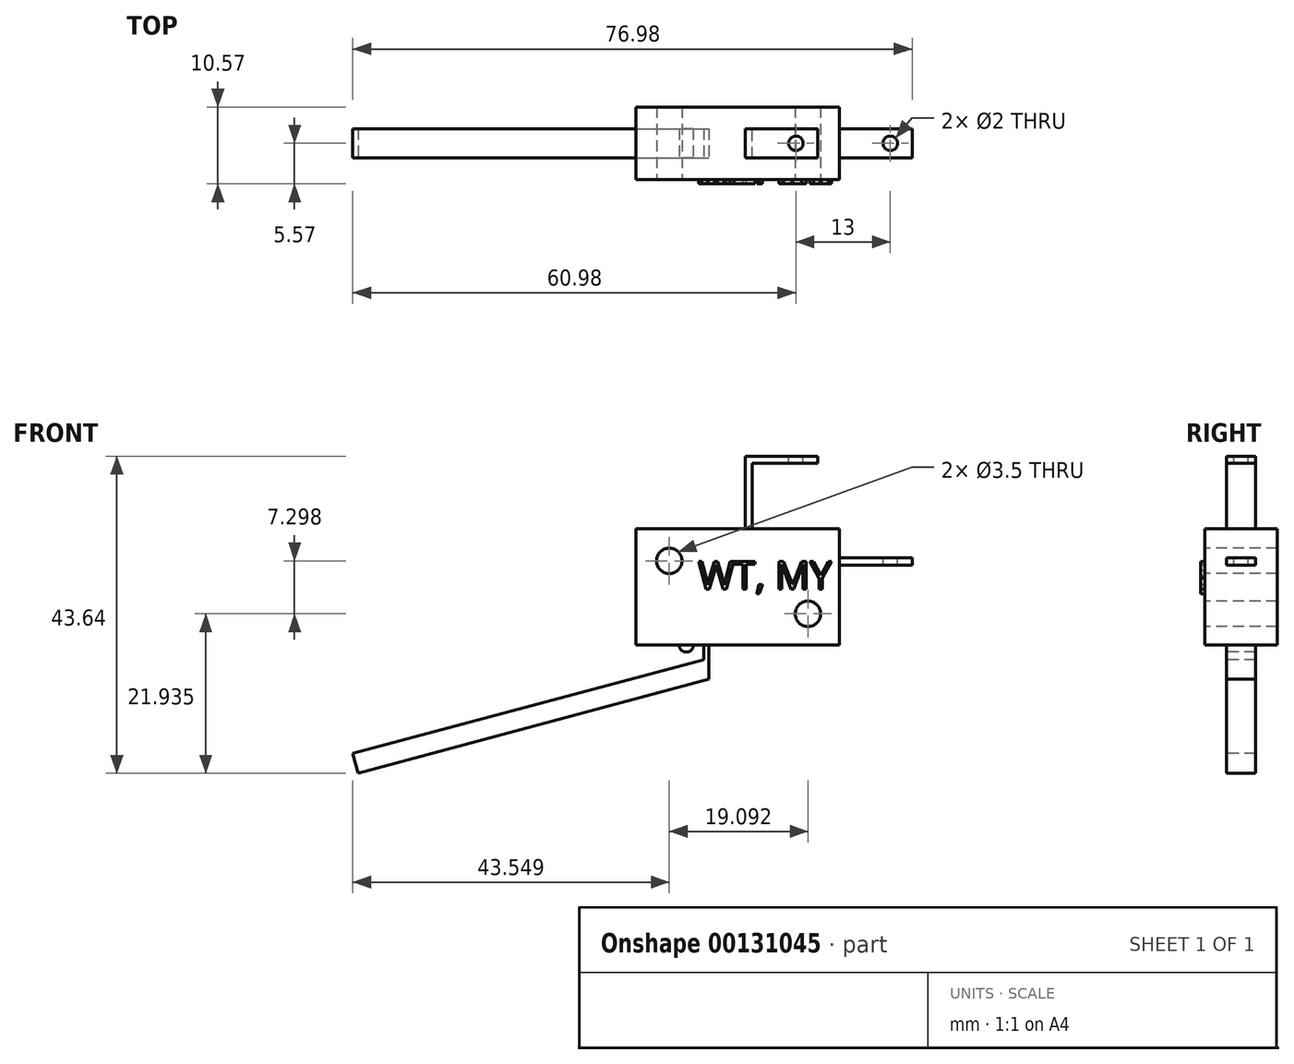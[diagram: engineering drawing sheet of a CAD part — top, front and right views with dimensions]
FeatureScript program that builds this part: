
annotation { "Feature Type Name" : "Feature", "Feature Type Description" : "" }
export const myFeature = defineFeature(function(context is Context, id is Id, definition is map)
    precondition{}
    {
        {
            var Q0;
            Q0=qCreatedBy(makeId("Front.planeOp"),FACE);
            var sketch = newSketch(context, id + "F0", { "sketchPlane" : qUnion([Q0])});
            skLineSegment(sketch, "E0.bottom", {"start": v(0, -16) * mm, "end": v(28, -16) * mm});
            skLineSegment(sketch, "E0.top", {"start": v(0, 0) * mm, "end": v(28, 0) * mm});
            skLineSegment(sketch, "E0.left", {"start": v(0, -16) * mm, "end": v(0, 0) * mm});
            skLineSegment(sketch, "E0.right", {"start": v(28, -16) * mm, "end": v(28, 0) * mm});
            skSolve(sketch);
        }
        {
            var Q0;
            Q0=qSketchRegion(id+"F0",true);
            extrude(context, id + "F1", {"entities" : qUnion([Q0]), "endBound" : BoundingType.SYMMETRIC, "depth" : 10 * mm});
        }
        {
            var Q0;
            Q0=makeQuery(id+"F1.opExtrude","CAP_FACE",FACE,{"disambiguationData":[OSD([sQuery(id+"F0.wireOp",EDGE,"E0.bottom"),sQuery(id+"F0.wireOp",EDGE,"E0.top"),sQuery(id+"F0.wireOp",EDGE,"E0.left"),sQuery(id+"F0.wireOp",EDGE,"E0.right")])],"isStart":false});
            var sketch = newSketch(context, id + "F2", { "sketchPlane" : qUnion([Q0])});
            skCircle(sketch, "E1", {"center": v(23.66, -11.7) * mm, "radius": 1.75 * mm});
            skCircle(sketch, "E2", {"center": v(4.57, -4.4) * mm, "radius": 1.75 * mm});
            skPoint(sketch, "E3", {"position": v(0, -8) * mm});
            skSolve(sketch);
        }
        {
            var Q0;
            Q0=makeQuery(id+"F2.imprint","IMPRINT",FACE,{"disambiguationData":[TD([[makeQuery(id+"F2.imprint","IMPRINT",EDGE,{"derivedFrom":sQuery(id+"F2.wireOp",EDGE,"E2")}),1.0]])]});
            var Q1;
            Q1=makeQuery(id+"F2.imprint","IMPRINT",FACE,{"disambiguationData":[TD([[makeQuery(id+"F2.imprint","IMPRINT",EDGE,{"derivedFrom":sQuery(id+"F2.wireOp",EDGE,"E1")}),1.0]])]});
            extrude(context, id + "F3", {"entities" : qUnion([Q0, Q1]), "operationType" : NewBodyOperationType.REMOVE, "endBound" : BoundingType.THROUGH_ALL, "oppositeDirection" : true, "depth" : 25 * mm});
        }
        {
            var Q0;
            Q0=makeQuery(id+"F1.opExtrude","SWEPT_FACE",FACE,{"disambiguationData":[OSD([sQuery(id+"F0.wireOp",EDGE,"E0.right")])]});
            var sketch = newSketch(context, id + "F4", { "sketchPlane" : qUnion([Q0])});
            skLineSegment(sketch, "E4.bottom", {"start": v(-2, -4) * mm, "end": v(2, -4) * mm});
            skLineSegment(sketch, "E4.top", {"start": v(-2, -5) * mm, "end": v(2, -5) * mm});
            skLineSegment(sketch, "E4.left", {"start": v(-2, -4) * mm, "end": v(-2, -5) * mm});
            skLineSegment(sketch, "E4.right", {"start": v(2, -4) * mm, "end": v(2, -5) * mm});
            skPoint(sketch, "E5", {"position": v(0, -5) * mm});
            skSolve(sketch);
        }
        {
            var Q0;
            Q0=qSketchRegion(id+"F4",true);
            extrude(context, id + "F5", {"entities" : qUnion([Q0]), "operationType" : NewBodyOperationType.ADD, "depth" : 10 * mm});
        }
        {
            var Q0;
            Q0=makeQuery(id+"F1.opExtrude","SWEPT_FACE",FACE,{"disambiguationData":[OSD([sQuery(id+"F0.wireOp",EDGE,"E0.top")])]});
            var sketch = newSketch(context, id + "F6", { "sketchPlane" : qUnion([Q0])});
            skLineSegment(sketch, "E6.bottom", {"start": v(15, -2) * mm, "end": v(16, -2) * mm});
            skLineSegment(sketch, "E6.top", {"start": v(15, 2) * mm, "end": v(16, 2) * mm});
            skLineSegment(sketch, "E6.left", {"start": v(15, -2) * mm, "end": v(15, 2) * mm});
            skLineSegment(sketch, "E6.right", {"start": v(16, -2) * mm, "end": v(16, 2) * mm});
            skSolve(sketch);
        }
        {
            var Q0;
            Q0=qSketchRegion(id+"F6",true);
            extrude(context, id + "F7", {"entities" : qUnion([Q0]), "operationType" : NewBodyOperationType.ADD, "depth" : 10 * mm});
        }
        {
            var Q0;
            Q0=makeQuery(id+"F7.opExtrude","SWEPT_FACE",FACE,{"disambiguationData":[OSD([sQuery(id+"F6.wireOp",EDGE,"E6.right")])]});
            var sketch = newSketch(context, id + "F8", { "sketchPlane" : qUnion([Q0])});
            skLineSegment(sketch, "E7.bottom", {"start": v(-2, 9) * mm, "end": v(2, 9) * mm});
            skLineSegment(sketch, "E7.top", {"start": v(-2, 10) * mm, "end": v(2, 10) * mm});
            skLineSegment(sketch, "E7.left", {"start": v(-2, 9) * mm, "end": v(-2, 10) * mm});
            skLineSegment(sketch, "E7.right", {"start": v(2, 9) * mm, "end": v(2, 10) * mm});
            skSolve(sketch);
        }
        {
            var Q0;
            Q0=qSketchRegion(id+"F8",true);
            extrude(context, id + "F9", {"entities" : qUnion([Q0]), "operationType" : NewBodyOperationType.ADD, "depth" : 9 * mm});
        }
        {
            var Q0;
            Q0=makeQuery(id+"F5.opExtrude","SWEPT_FACE",FACE,{"disambiguationData":[OSD([sQuery(id+"F4.wireOp",EDGE,"E4.bottom")])]});
            var sketch = newSketch(context, id + "F10", { "sketchPlane" : qUnion([Q0])});
            skCircle(sketch, "E8", {"center": v(35, 0) * mm, "radius": 1 * mm});
            skPoint(sketch, "E9", {"position": v(38, 0) * mm});
            skSolve(sketch);
        }
        {
            var Q0;
            Q0=qSketchRegion(id+"F10",true);
            extrude(context, id + "F11", {"entities" : qUnion([Q0]), "operationType" : NewBodyOperationType.REMOVE, "endBound" : BoundingType.THROUGH_ALL, "oppositeDirection" : true, "depth" : 25 * mm});
        }
        {
            var Q0;
            Q0=makeQuery(id+"F9.boolean.opBoolean","MERGE",FACE,{"derivedFrom":[makeQuery(id+"F7.opExtrude","CAP_FACE",FACE,{"disambiguationData":[OSD([sQuery(id+"F6.wireOp",EDGE,"E6.bottom"),sQuery(id+"F6.wireOp",EDGE,"E6.top"),sQuery(id+"F6.wireOp",EDGE,"E6.left"),sQuery(id+"F6.wireOp",EDGE,"E6.right")])],"isStart":false}),makeQuery(id+"F9.opExtrude","SWEPT_FACE",FACE,{"disambiguationData":[OSD([sQuery(id+"F8.wireOp",EDGE,"E7.top")])]})]});
            var sketch = newSketch(context, id + "F12", { "sketchPlane" : qUnion([Q0])});
            skCircle(sketch, "E10", {"center": v(22, 0) * mm, "radius": 1 * mm});
            skPoint(sketch, "E11", {"position": v(25, 0) * mm});
            skSolve(sketch);
        }
        {
            var Q0;
            Q0=qSketchRegion(id+"F12",true);
            extrude(context, id + "F13", {"entities" : qUnion([Q0]), "operationType" : NewBodyOperationType.REMOVE, "endBound" : BoundingType.UP_TO_NEXT, "oppositeDirection" : true, "depth" : 25 * mm});
        }
        {
            var Q0;
            Q0=makeQuery(id+"F1.opExtrude","SWEPT_FACE",FACE,{"disambiguationData":[OSD([sQuery(id+"F0.wireOp",EDGE,"E0.bottom")])]});
            var sketch = newSketch(context, id + "F14", { "sketchPlane" : qUnion([Q0])});
            skLineSegment(sketch, "E12.bottom", {"start": v(6.91, -2) * mm, "end": v(7.89, -2) * mm});
            skLineSegment(sketch, "E12.top", {"start": v(6.91, 2) * mm, "end": v(7.89, 2) * mm});
            skLineSegment(sketch, "E12.left", {"start": v(7.89, -2) * mm, "end": v(7.89, 2) * mm});
            skLineSegment(sketch, "E12.right", {"start": v(6.91, -2) * mm, "end": v(6.91, 2) * mm});
            skLineSegment(sketch, "E13.bottom", {"start": v(9.31, -2) * mm, "end": v(10.04, -2) * mm});
            skLineSegment(sketch, "E13.top", {"start": v(9.31, 2) * mm, "end": v(10.04, 2) * mm});
            skLineSegment(sketch, "E13.left", {"start": v(9.31, -2) * mm, "end": v(9.31, 2) * mm});
            skLineSegment(sketch, "E13.right", {"start": v(10.04, -2) * mm, "end": v(10.04, 2) * mm});
            skPoint(sketch, "E14", {"position": v(7.89, 0) * mm});
            skPoint(sketch, "E15", {"position": v(9.31, 0) * mm});
            skSolve(sketch);
        }
        {
            var Q0;
            Q0=makeQuery(id+"F14.imprint","IMPRINT",FACE,{"disambiguationData":[TD([[makeQuery(id+"F14.imprint","IMPRINT",EDGE,{"derivedFrom":sQuery(id+"F14.wireOp",EDGE,"E12.bottom")}),1.0]])]});
            var Q1;
            Q1=sQuery(id+"F14.wireOp",EDGE,"E12.right");
            revolve(context, id + "F15", {"operationType" : NewBodyOperationType.ADD, "entities" : qUnion([Q0]), "axis" : qUnion([Q1]), "revolveType" : RevolveType.ONE_DIRECTION, "oppositeDirection" : true, "angle" : 180 * degree});
        }
        {
            var Q0;
            Q0=makeQuery(id+"F14.imprint","IMPRINT",FACE,{"disambiguationData":[TD([[makeQuery(id+"F14.imprint","IMPRINT",EDGE,{"derivedFrom":sQuery(id+"F14.wireOp",EDGE,"E13.bottom")}),1.0]])]});
            extrude(context, id + "F16", {"entities" : qUnion([Q0]), "operationType" : NewBodyOperationType.ADD, "depth" : 5 * mm});
        }
        {
            var Q0;
            Q0=makeQuery(id+"F16.opExtrude","CAP_EDGE",EDGE,{"disambiguationData":[OSD([sQuery(id+"F14.wireOp",EDGE,"E13.left")])],"isStart":false});
            chamfer(context, id + "F17", {"entities" : qUnion([Q0]), "chamferType" : ChamferType.OFFSET_ANGLE, "width" : 3 * mm, "oppositeDirection" : false, "angle" : 15 * degree, "tangentPropagation" : true});
        }
        {
            var Q0;
            Q0=makeQuery(id+"F17.opChamfer","BLEND_FACE",FACE,{"disambiguationData":[OSD([sQuery(id+"F14.wireOp",EDGE,"E13.left")])]});
            extrude(context, id + "F18", {"entities" : qUnion([Q0]), "operationType" : NewBodyOperationType.ADD, "depth" : 50 * mm});
        }
        {
            var Q0;
            Q0=makeQuery(id+"F1.opExtrude","CAP_FACE",FACE,{"disambiguationData":[OSD([sQuery(id+"F0.wireOp",EDGE,"E0.bottom"),sQuery(id+"F0.wireOp",EDGE,"E0.top"),sQuery(id+"F0.wireOp",EDGE,"E0.left"),sQuery(id+"F0.wireOp",EDGE,"E0.right")])],"isStart":false});
            var sketch = newSketch(context, id + "F19", { "sketchPlane" : qUnion([Q0])});
            skText(sketch, "E16", { "text": "WT, MY", "fontName": "OpenSans-Regular.ttf"});
            const initialGuessF19  = {"E16": [0.00855, -0.00828, 1, 0, 0.00384]};
            skSetInitialGuess(sketch, initialGuessF19);
            skSolve(sketch);
        }
        {
            var Q0;
            Q0=qSketchRegion(id+"F19",true);
            extrude(context, id + "F20", {"entities" : qUnion([Q0]), "operationType" : NewBodyOperationType.ADD, "depth" : 0.57 * mm});
        }
    });
